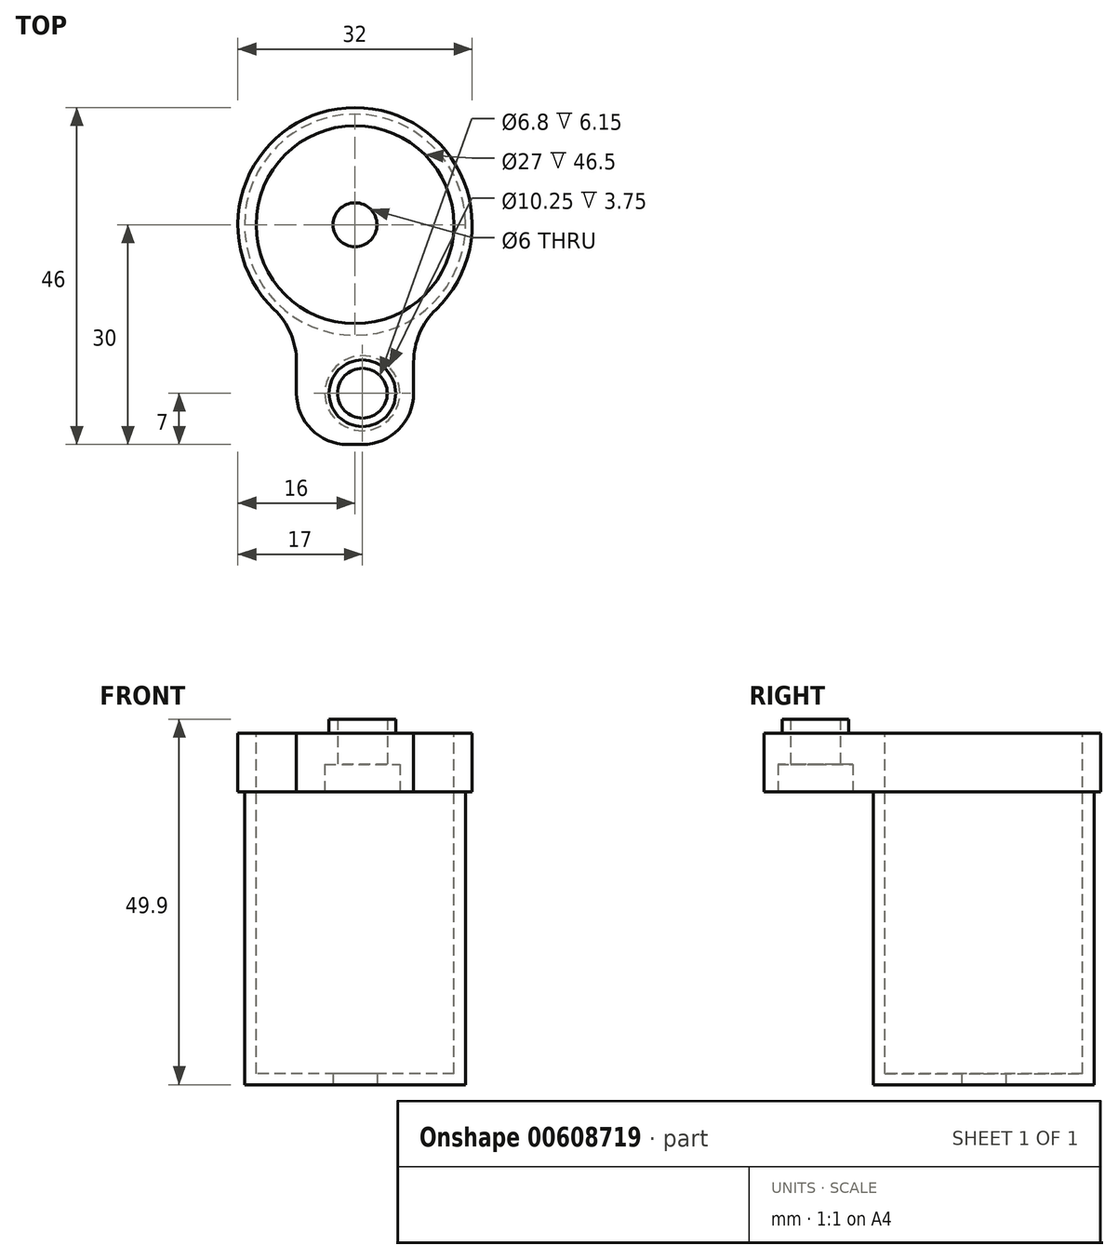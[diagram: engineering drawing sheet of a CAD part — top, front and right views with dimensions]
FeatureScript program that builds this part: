
annotation { "Feature Type Name" : "Feature", "Feature Type Description" : "" }
export const myFeature = defineFeature(function(context is Context, id is Id, definition is map)
    precondition{}
    {
        {
            var Q0;
            Q0=qCreatedBy(makeId("Top.planeOp"),FACE);
            var sketch = newSketch(context, id + "F0", { "sketchPlane" : qUnion([Q0])});
            skCircle(sketch, "E0", {"center": v(0, 0) * mm, "radius": 16 * mm});
            skLineSegment(sketch, "E1.bottom", {"start": v(-8, 0) * mm, "end": v(8, 0) * mm});
            skLineSegment(sketch, "E1.top", {"start": v(-8, -30) * mm, "end": v(8, -30) * mm});
            skLineSegment(sketch, "E1.left", {"start": v(-8, 0) * mm, "end": v(-8, -30) * mm});
            skLineSegment(sketch, "E1.right", {"start": v(8, 0) * mm, "end": v(8, -30) * mm});
            skSolve(sketch);
        }
        {
            var Q0;
            Q0 = qSketchRegion(id + "F0", true);
            extrude(context, id + "F1", {"entities" : qUnion([Q0]), "depth" : 8 * mm, "offsetDistance" : 25 * mm});
        }
        {
            var Q0;
            Q0=makeQuery(id+"F1.opExtrude","CAP_FACE",FACE,{"disambiguationData":[OSD([sQuery(id+"F0.wireOp",EDGE,"E0"),sQuery(id+"F0.wireOp",EDGE,"E1.top"),sQuery(id+"F0.wireOp",EDGE,"E1.left"),sQuery(id+"F0.wireOp",EDGE,"E1.right")])],"isStart":true});
            var sketch = newSketch(context, id + "F2", { "sketchPlane" : qUnion([Q0])});
            skCircle(sketch, "E2", {"center": v(0, 0) * mm, "radius": 15.1 * mm});
            skSolve(sketch);
        }
        {
            var Q0;
            {var subQ0=sQuery(id+"F2.wireOp",EDGE,"E2");Q0=makeQuery(id+"F2.imprint","IMPRINT",FACE,{"disambiguationData":[TD([[makeQuery(id+"F2.imprint","IMPRINT",EDGE,{"disambiguationData":[OD(0.0)],"derivedFrom":subQ0}),1.0]])]});}
            extrude(context, id + "F3", {"entities" : qUnion([Q0]), "operationType" : NewBodyOperationType.ADD, "depth" : 40 * mm, "offsetDistance" : 25 * mm});
        }
        {
            var Q0;
            Q0=makeQuery(id+"F1.opExtrude","SWEPT_EDGE",EDGE,{"disambiguationData":[OSD([sQuery(id+"F0.wireOp",EDGE,"E1.top"),sQuery(id+"F0.wireOp",EDGE,"E1.left")])]});
            var Q1;
            Q1=makeQuery(id+"F1.opExtrude","SWEPT_EDGE",EDGE,{"disambiguationData":[OSD([sQuery(id+"F0.wireOp",EDGE,"E1.top"),sQuery(id+"F0.wireOp",EDGE,"E1.right")])]});
            fillet(context, id + "F4", {"entities" : qUnion([Q0, Q1]), "radius" : 7 * mm, "tangentPropagation" : true, "allowEdgeOverflow" : false});
        }
        {
            var Q0;
            Q0=makeQuery(id+"F1.opExtrude","CAP_FACE",FACE,{"disambiguationData":[OSD([sQuery(id+"F0.wireOp",EDGE,"E0"),sQuery(id+"F0.wireOp",EDGE,"E1.top"),sQuery(id+"F0.wireOp",EDGE,"E1.left"),sQuery(id+"F0.wireOp",EDGE,"E1.right")])],"isStart":false});
            var sketch = newSketch(context, id + "F5", { "sketchPlane" : qUnion([Q0])});
            skCircle(sketch, "E3", {"center": v(0, 0) * mm, "radius": 13.5 * mm});
            skSolve(sketch);
        }
        {
            var Q0;
            Q0=makeQuery(id+"F5.imprint","IMPRINT",FACE,{"disambiguationData":[TD([[makeQuery(id+"F5.imprint","IMPRINT",EDGE,{"derivedFrom":sQuery(id+"F5.wireOp",EDGE,"E3")}),1.0]])]});
            extrude(context, id + "F6", {"entities" : qUnion([Q0]), "operationType" : NewBodyOperationType.REMOVE, "oppositeDirection" : true, "depth" : 46.5 * mm, "offsetDistance" : 25 * mm});
        }
        {
            var Q0;
            Q0=makeQuery(id+"F1.opExtrude","CAP_FACE",FACE,{"disambiguationData":[OSD([sQuery(id+"F0.wireOp",EDGE,"E0"),sQuery(id+"F0.wireOp",EDGE,"E1.top"),sQuery(id+"F0.wireOp",EDGE,"E1.left"),sQuery(id+"F0.wireOp",EDGE,"E1.right")])],"isStart":false});
            var sketch = newSketch(context, id + "F7", { "sketchPlane" : qUnion([Q0])});
            skCircle(sketch, "E4", {"center": v(1, -23) * mm, "radius": 3.4 * mm});
            skCircle(sketch, "E5", {"center": v(1, -23) * mm, "radius": 4.55 * mm});
            skSolve(sketch);
        }
        {
            var Q0;
            Q0=makeQuery(id+"F7.imprint","IMPRINT",FACE,{"disambiguationData":[TD([[makeQuery(id+"F7.imprint","IMPRINT",EDGE,{"derivedFrom":sQuery(id+"F7.wireOp",EDGE,"E4")}),-1.0]])]});
            extrude(context, id + "F8", {"entities" : qUnion([Q0]), "operationType" : NewBodyOperationType.ADD, "depth" : 1.9 * mm, "offsetDistance" : 25 * mm});
        }
        {
            var Q0;
            Q0=makeQuery(id+"F8.boolean.opBoolean","SPLIT",FACE,{"disambiguationData":[TD([makeQuery(id+"F8.opExtrude","SWEPT_FACE",FACE,{"disambiguationData":[OSD([sQuery(id+"F7.wireOp",EDGE,"E4")])]})])],"derivedFrom":makeQuery(id+"F1.opExtrude","CAP_FACE",FACE,{"disambiguationData":[OSD([sQuery(id+"F0.wireOp",EDGE,"E0"),sQuery(id+"F0.wireOp",EDGE,"E1.top"),sQuery(id+"F0.wireOp",EDGE,"E1.left"),sQuery(id+"F0.wireOp",EDGE,"E1.right")])],"isStart":false})});
            extrude(context, id + "F9", {"entities" : qUnion([Q0]), "operationType" : NewBodyOperationType.REMOVE, "endBound" : BoundingType.THROUGH_ALL, "oppositeDirection" : true, "depth" : 25 * mm, "offsetDistance" : 25 * mm});
        }
        {
            var Q0;
            Q0=makeQuery(id+"F1.opExtrude","CAP_FACE",FACE,{"disambiguationData":[OSD([sQuery(id+"F0.wireOp",EDGE,"E0"),sQuery(id+"F0.wireOp",EDGE,"E1.top"),sQuery(id+"F0.wireOp",EDGE,"E1.left"),sQuery(id+"F0.wireOp",EDGE,"E1.right")])],"isStart":true});
            var sketch = newSketch(context, id + "F10", { "sketchPlane" : qUnion([Q0])});
            skCircle(sketch, "E6", {"center": v(1, 23) * mm, "radius": 5.12 * mm});
            skSolve(sketch);
        }
        {
            var Q0;
            Q0=makeQuery(id+"F10.imprint","IMPRINT",FACE,{"disambiguationData":[TD([[makeQuery(id+"F10.imprint","IMPRINT",EDGE,{"derivedFrom":sQuery(id+"F10.wireOp",EDGE,"E6")}),1.0]])]});
            extrude(context, id + "F11", {"entities" : qUnion([Q0]), "operationType" : NewBodyOperationType.REMOVE, "oppositeDirection" : true, "depth" : 3.75 * mm, "offsetDistance" : 25 * mm});
        }
        {
            var Q0;
            Q0=makeQuery(id+"F3.opExtrude","CAP_FACE",FACE,{"disambiguationData":[OSD([sQuery(id+"F2.wireOp",EDGE,"E2")])],"isStart":false});
            var sketch = newSketch(context, id + "F12", { "sketchPlane" : qUnion([Q0])});
            skCircle(sketch, "E7", {"center": v(0, 0) * mm, "radius": 3 * mm});
            skSolve(sketch);
        }
        {
            var Q0;
            Q0 = qSketchRegion(id + "F12", true);
            extrude(context, id + "F13", {"entities" : qUnion([Q0]), "operationType" : NewBodyOperationType.REMOVE, "endBound" : BoundingType.THROUGH_ALL, "oppositeDirection" : true, "depth" : 25 * mm, "offsetDistance" : 25 * mm});
        }
        {
            var Q0;
            Q0=makeQuery(id+"F1.opExtrude","SWEPT_EDGE",EDGE,{"disambiguationData":[OSD([sQuery(id+"F0.wireOp",EDGE,"E0"),sQuery(id+"F0.wireOp",EDGE,"E1.left")])]});
            var Q1;
            Q1=makeQuery(id+"F1.opExtrude","SWEPT_EDGE",EDGE,{"disambiguationData":[OSD([sQuery(id+"F0.wireOp",EDGE,"E0"),sQuery(id+"F0.wireOp",EDGE,"E1.right")])]});
            fillet(context, id + "F14", {"entities" : qUnion([Q0, Q1]), "radius" : 10 * mm, "tangentPropagation" : true, "allowEdgeOverflow" : false});
        }
    });
